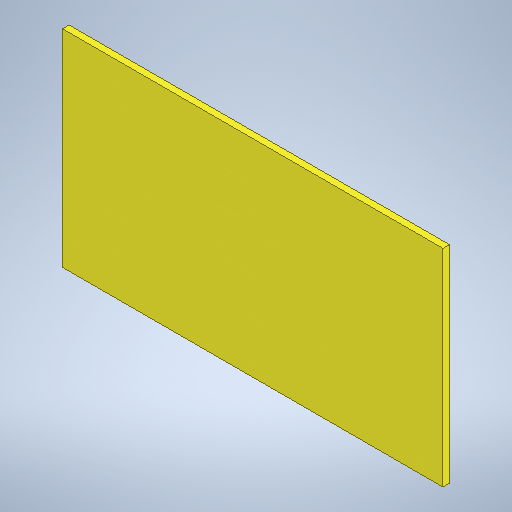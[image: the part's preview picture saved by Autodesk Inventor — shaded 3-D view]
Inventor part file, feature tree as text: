
AUTODESK INVENTOR PART (.ipt)
format: ipt  version: 2025.1 (Build 291241020, 241B)  size: 233,472 bytes
history: native  units: in
note: dims shown in document units (in); Inventor stores cm internally (conversion verified against a paired STEP export)
features: extrude x1, sketch x1
ambient origin geometry x8: Origin, YZ Plane, XZ Plane, XY Plane, X Axis, Y Axis, Z Axis, Center Point
bodies: Solid1 (feature_tree)
feature tree (2):
  extrude  "Extrusion1"  Depth=36.5in
  sketch  "Sketch1"  dims[d2=19.831in d3=36.5in d4=0.625in d5=0.0in]
